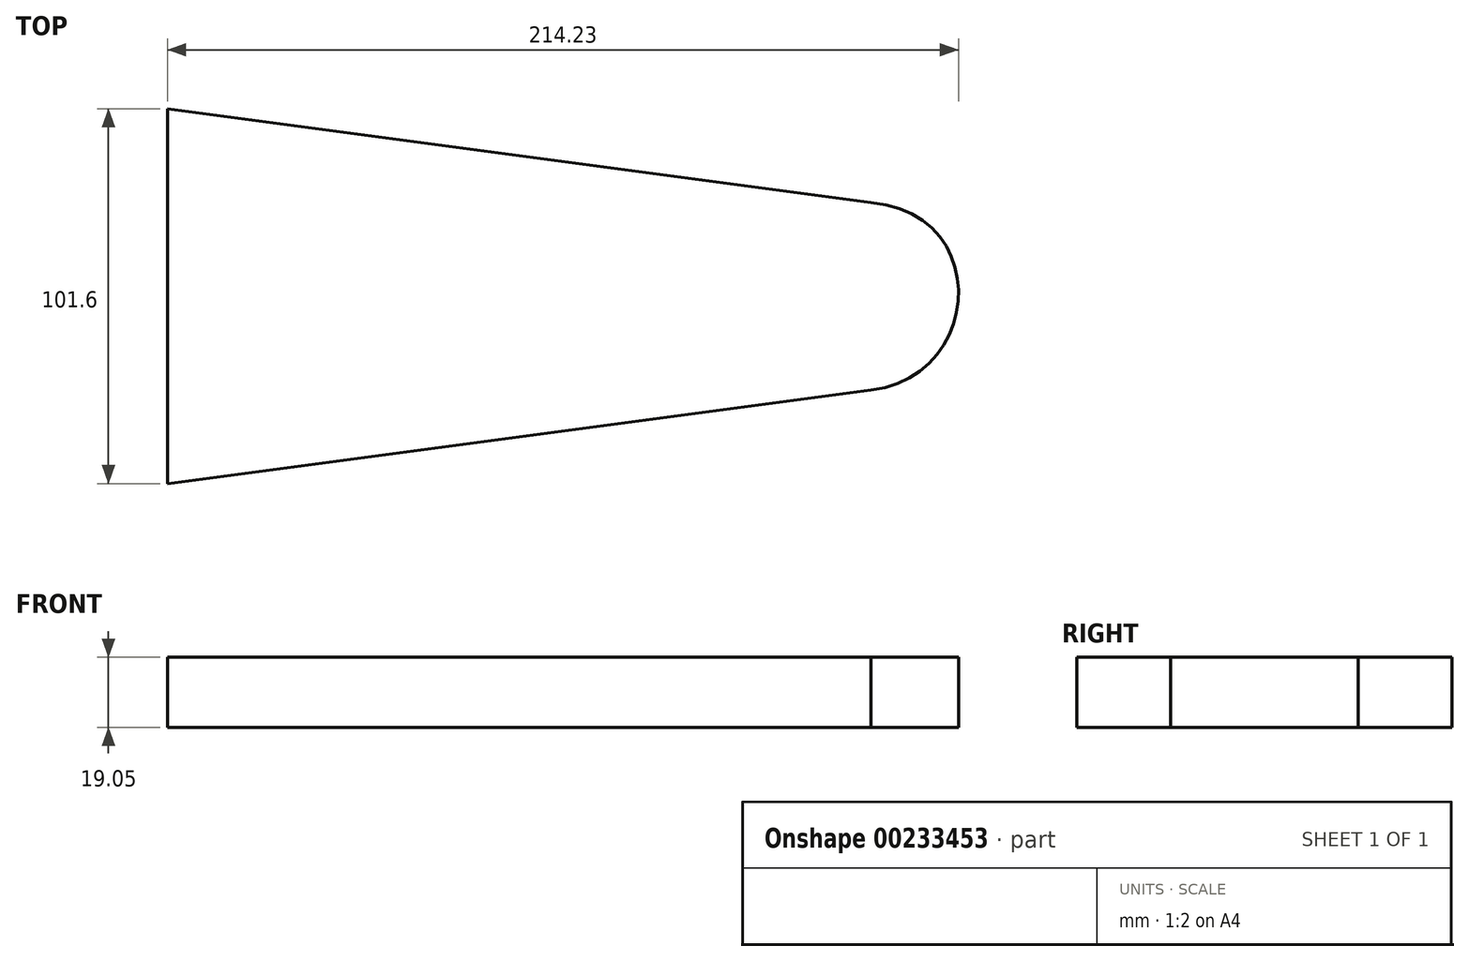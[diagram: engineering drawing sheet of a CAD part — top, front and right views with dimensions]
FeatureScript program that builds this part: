
annotation { "Feature Type Name" : "Feature", "Feature Type Description" : "" }
export const myFeature = defineFeature(function(context is Context, id is Id, definition is map)
    precondition{}
    {
        {
            var Q0;
            Q0=qCreatedBy(makeId("Top.planeOp"),FACE);
            var sketch = newSketch(context, id + "F0", { "sketchPlane" : qUnion([Q0])});
            skLineSegment(sketch, "E0.left", {"start": v(-107.95, -50.8) * mm, "end": v(-107.95, 50.8) * mm});
            skPoint(sketch, "E0.middle", {"position": v(0, 0) * mm});
            skLineSegment(sketch, "E1", {"start": v(82.55, -25.4) * mm, "end": v(-107.95, -50.8) * mm});
            skLineSegment(sketch, "E2", {"start": v(-107.95, 50.8) * mm, "end": v(82.55, 25.4) * mm});
            skFitSpline(sketch, "E3", {"points": [v(82.55, 25.4) * mm, v(82.55, -25.4) * mm], "startDerivative": vector(98.87, -8.26) * mm, "endDerivative": vector(-90.87, -10.04) * mm});
            skSolve(sketch);
        }
        {
            var Q0;
            Q0 = qSketchRegion(id + "F0", true);
            extrude(context, id + "F1", {"entities" : qUnion([Q0]), "depth" : 19.05 * mm});
        }
    });
